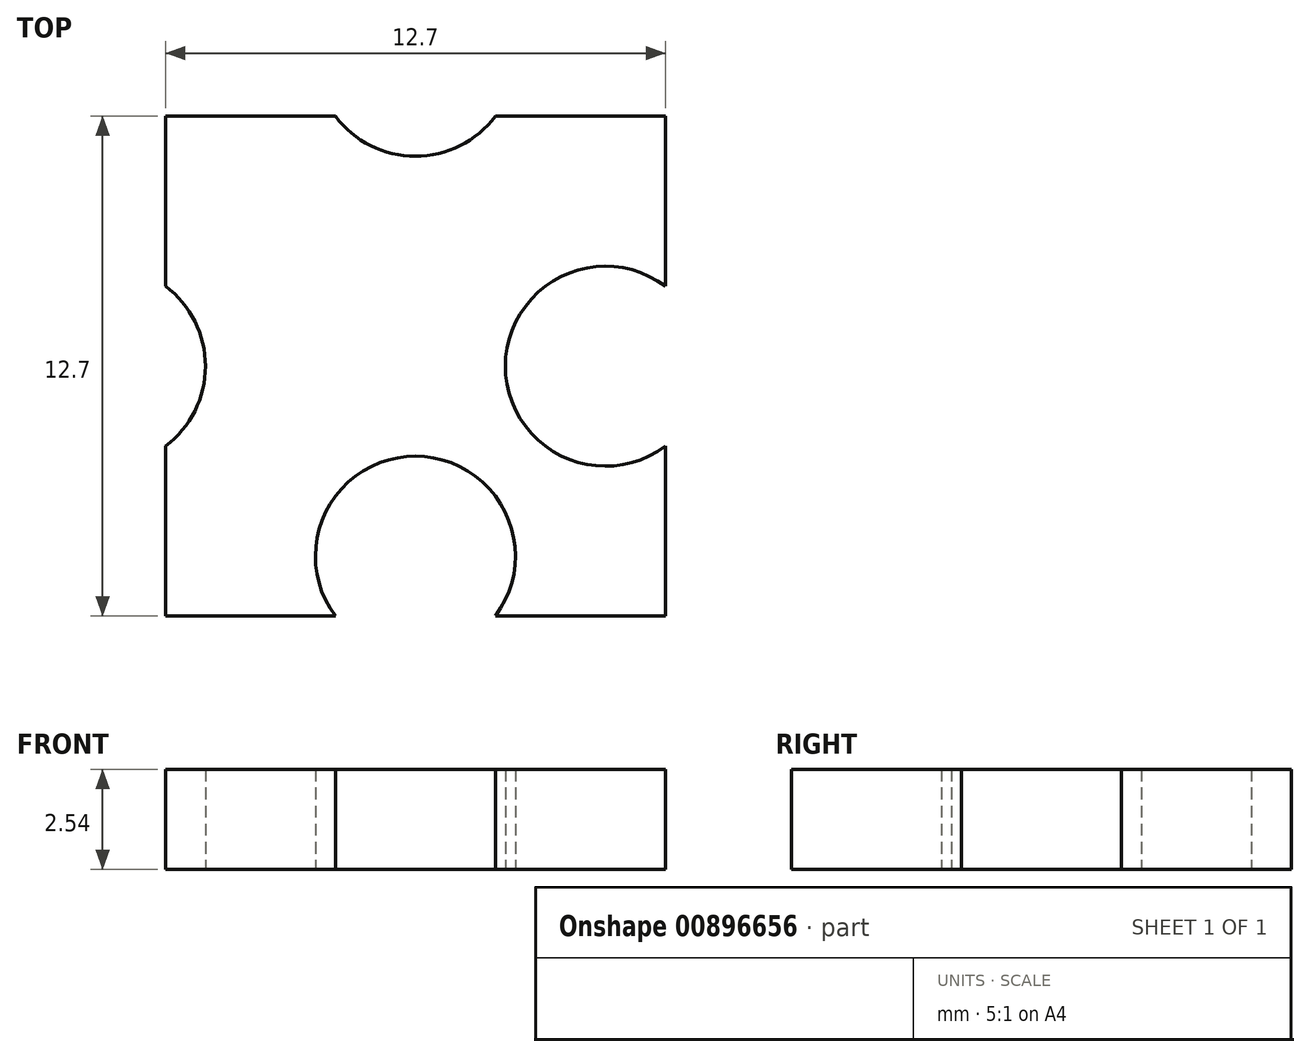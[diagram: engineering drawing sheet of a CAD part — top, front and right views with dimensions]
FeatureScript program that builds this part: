
annotation { "Feature Type Name" : "Feature", "Feature Type Description" : "" }
export const myFeature = defineFeature(function(context is Context, id is Id, definition is map)
    precondition{}
    {
        {
            var Q0;
            Q0=qCreatedBy(makeId("Top.planeOp"),FACE);
            var sketch = newSketch(context, id + "F0", { "sketchPlane" : qUnion([Q0])});
            skLineSegment(sketch, "E0.bottom", {"start": v(-49.96, 25.09) * mm, "end": v(-37.26, 25.09) * mm});
            skLineSegment(sketch, "E0.top", {"start": v(-49.96, 12.39) * mm, "end": v(-37.26, 12.39) * mm});
            skLineSegment(sketch, "E0.left", {"start": v(-49.96, 25.09) * mm, "end": v(-49.96, 12.39) * mm});
            skLineSegment(sketch, "E0.right", {"start": v(-37.26, 25.09) * mm, "end": v(-37.26, 12.39) * mm});
            skCircle(sketch, "E1", {"center": v(-51.49, 18.74) * mm, "radius": 2.54 * mm});
            skLineSegment(sketch, "E2", {"start": v(-49.96, 18.74) * mm, "end": v(-71.75, 18.74) * mm, "construction": true});
            skLineSegment(sketch, "E3", {"start": v(-43.61, 25.09) * mm, "end": v(-43.61, 12.39) * mm, "construction": true});
            skLineSegment(sketch, "E4", {"start": v(-49.96, 18.74) * mm, "end": v(-37.26, 18.74) * mm, "construction": true});
            skCircle(sketch, "E5.1.0", {"center": v(-43.61, 26.6) * mm, "radius": 2.54 * mm});
            skPoint(sketch, "E5.center", {"position": v(-43.61, 18.74) * mm});
            skLineSegment(sketch, "E5.anchor1", {"start": v(-43.61, 18.74) * mm, "end": v(-51.49, 18.74) * mm, "construction": true});
            skLineSegment(sketch, "E5.anchor2", {"start": v(-43.61, 18.74) * mm, "end": v(-43.61, 26.6) * mm, "construction": true});
            skCircle(sketch, "E6", {"center": v(-38.79, 18.74) * mm, "radius": 2.54 * mm});
            skLineSegment(sketch, "E7", {"start": v(-37.26, 18.74) * mm, "end": v(-26.26, 18.74) * mm, "construction": true});
            skCircle(sketch, "E8.1.0", {"center": v(-43.61, 13.9) * mm, "radius": 2.54 * mm});
            skLineSegment(sketch, "E8.anchor1", {"start": v(-43.61, 18.74) * mm, "end": v(-38.79, 18.74) * mm, "construction": true});
            skLineSegment(sketch, "E8.anchor2", {"start": v(-43.61, 18.74) * mm, "end": v(-43.61, 13.9) * mm, "construction": true});
            skSolve(sketch);
        }
        {
            var Q0;
            {var subQ0=sQuery(id+"F0.wireOp",EDGE,"E1");var subQ1=sQuery(id+"F0.wireOp",EDGE,"E0.left");var subQ2=makeQuery(id+"F0.imprint","INTERSECT",VERTEX,{"disambiguationData":[OD(0.0)],"derivedFrom":[subQ1,subQ0]});Q0=makeQuery(id+"F0.imprint","IMPRINT",FACE,{"disambiguationData":[TD([[makeQuery(id+"F0.imprint","IMPRINT",EDGE,{"disambiguationData":[TD([[subQ2,-1.0]])],"derivedFrom":subQ1}),-1.0]])]});}
            var Q1;
            {var subQ0=sQuery(id+"F0.wireOp",EDGE,"E1");var subQ1=sQuery(id+"F0.wireOp",EDGE,"E0.left");var subQ2=makeQuery(id+"F0.imprint","INTERSECT",VERTEX,{"disambiguationData":[OD(0.0)],"derivedFrom":[subQ1,subQ0]});Q1=makeQuery(id+"F0.imprint","IMPRINT",FACE,{"disambiguationData":[TD([[makeQuery(id+"F0.imprint","IMPRINT",EDGE,{"disambiguationData":[TD([[subQ2,-1.0]])],"derivedFrom":subQ1}),1.0]])]});}
            var Q2;
            {var subQ1=sQuery(id+"F0.wireOp",EDGE,"E0.bottom");var subQ8=sQuery(id+"F0.wireOp",EDGE,"E0.left");var subQ13=makeQuery(id+"F0.imprint","INTERSECT",VERTEX,{"derivedFrom":[subQ1,subQ8]});Q2=makeQuery(id+"F0.imprint","IMPRINT",FACE,{"disambiguationData":[TD([[makeQuery(id+"F0.imprint","IMPRINT",EDGE,{"disambiguationData":[TD([[subQ13,-1.0]])],"derivedFrom":subQ1}),-1.0]])]});}
            var Q3;
            {var subQ0=sQuery(id+"F0.wireOp",EDGE,"E5.1.0");var subQ1=sQuery(id+"F0.wireOp",EDGE,"E0.bottom");var subQ2=makeQuery(id+"F0.imprint","INTERSECT",VERTEX,{"disambiguationData":[OD(0.0)],"derivedFrom":[subQ1,subQ0]});Q3=makeQuery(id+"F0.imprint","IMPRINT",FACE,{"disambiguationData":[TD([[makeQuery(id+"F0.imprint","IMPRINT",EDGE,{"disambiguationData":[TD([[subQ2,-1.0]])],"derivedFrom":subQ1}),-1.0]])]});}
            var Q4;
            {var subQ0=sQuery(id+"F0.wireOp",EDGE,"E5.1.0");var subQ1=sQuery(id+"F0.wireOp",EDGE,"E0.bottom");var subQ2=makeQuery(id+"F0.imprint","INTERSECT",VERTEX,{"disambiguationData":[OD(0.0)],"derivedFrom":[subQ1,subQ0]});Q4=makeQuery(id+"F0.imprint","IMPRINT",FACE,{"disambiguationData":[TD([[makeQuery(id+"F0.imprint","IMPRINT",EDGE,{"disambiguationData":[TD([[subQ2,-1.0]])],"derivedFrom":subQ1}),1.0]])]});}
            extrude(context, id + "F1", {"entities" : qUnion([Q0, Q1, Q2, Q3, Q4]), "depth" : 2.54 * mm, "offsetDistance" : 25.4 * mm});
        }
    });
